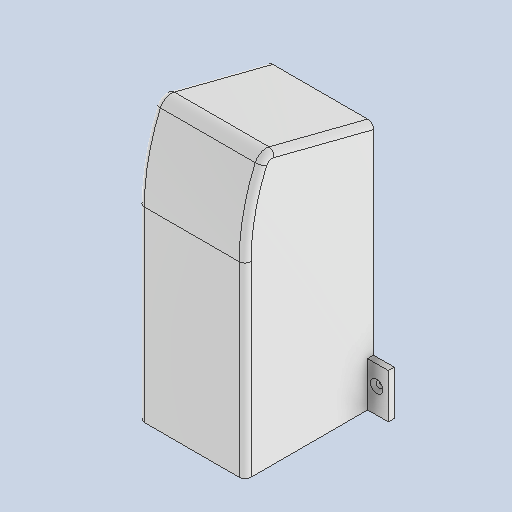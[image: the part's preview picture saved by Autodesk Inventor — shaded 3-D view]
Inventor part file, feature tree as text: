
AUTODESK INVENTOR PART (.ipt)
format: ipt  version: 2025 (Build 290162010, 162A)  size: 241,152 bytes
history: native  units: mm
features: other x7, extrude x6, sketch x6, reference x5, chamfer x2, projected_geometry x2, fillet x1
ambient origin geometry x8: Origin, YZ Plane, XZ Plane, XY Plane, X Axis, Y Axis, Z Axis, Center Point
bodies: Volumenkörper1 (feature_tree)
feature tree (29):
  extrude  "Extrusion1"  Depth=3.0mm
  extrude  "Extrusion2"  Depth=34.0mm TaperAngle=0.0deg
  extrude  "Extrusion3"  Depth=2.0mm
  sketch  "Skizze6"  dims[d20=15.0mm]
  fillet  "Rundung1"  Radius=7.0mm
  extrude  "Extrusion4"  Depth=7.0mm
  chamfer  "Fasen1"  Distance=2.2mm
  chamfer  "Fasen2"  Distance=2.0mm
  extrude  "Extrusion7"  Depth=1.0mm TaperAngle=45.0deg
  extrude  "Extrusion8"  Depth=1.0mm TaperAngle=45.0deg
  sketch  "Skizze1"  dims[d3=83.0mm d4=3.0mm]
  reference  "Referenz7"
  reference  "Referenz8"
  reference  "Referenz9"
  sketch  "Skizze2"  dims[d5=35.0mm d6=0.0mm d12=34.0mm d13=0.0mm]
  sketch  "Skizze3"  dims[d14=1.0mm d15=0.0mm d16=2.0mm d17=7.0mm]
  projected_geometry  "Projizierte Kontur2"
  sketch  "Skizze4"  dims[d18=15.0mm d19=7.0mm]
  reference  "Referenz10"
  reference  "Referenz11"
  projected_geometry  "Projizierte Kontur3"
  sketch  "Skizze8"  dims[d21=2.2mm d22=2.2mm d23=2.0mm d24=0.0mm d25=1.0mm d26=2.0mm d27=45.0deg d28=1.0mm d29=2.0mm d30=45.0deg d40=10.0mm d41=45.0deg d42=6.0mm d43=0.0mm d44=10.0mm d45=45.0deg d46=6.0mm d47=0.0mm]
  other  "<userpath>\GIT\HDVKBM\CAD\Krandemonstrator\Demonstrator.iam"
  other  "Demonstrator.iam"
  other  "Bedienhebel:1"
  other  "HebelhalterBlockBlind:1"
  other  "ISO 12633-2 - 20x20x2 - 200:1"
  other  "Schlitten:1"
  other  "SchlittenS:1"
